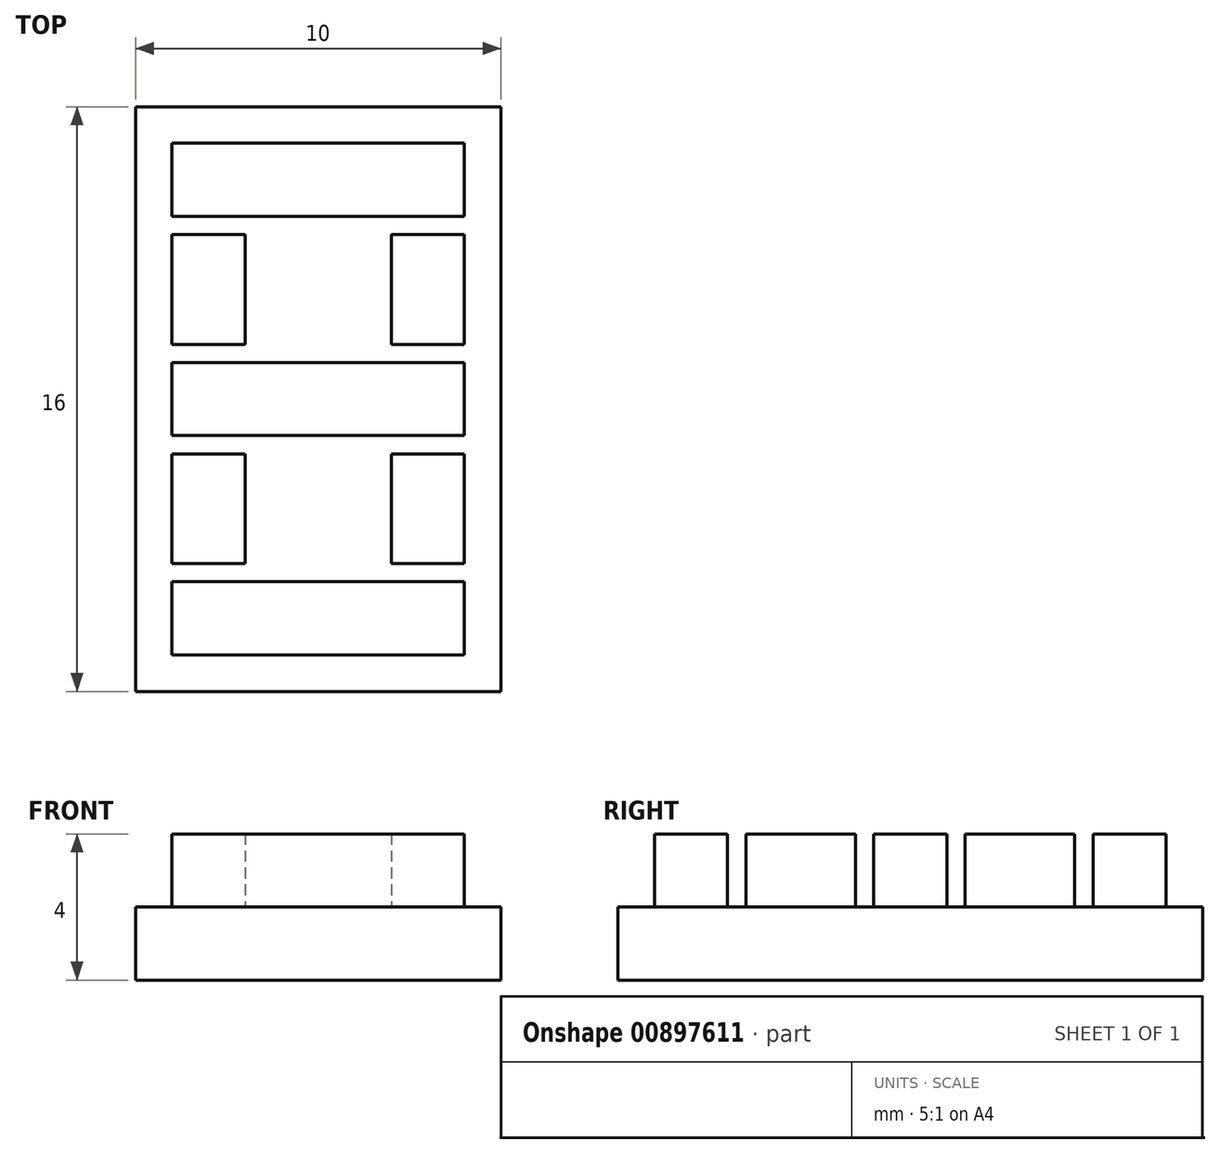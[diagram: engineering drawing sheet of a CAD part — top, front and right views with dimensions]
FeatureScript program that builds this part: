
annotation { "Feature Type Name" : "Feature", "Feature Type Description" : "" }
export const myFeature = defineFeature(function(context is Context, id is Id, definition is map)
    precondition{}
    {
        {
            var Q0;
            Q0=qCreatedBy(makeId("Top.planeOp"),FACE);
            var sketch = newSketch(context, id + "F0", { "sketchPlane" : qUnion([Q0])});
            skLineSegment(sketch, "E0.bottom", {"start": v(5, -8) * mm, "end": v(-5, -8) * mm});
            skLineSegment(sketch, "E0.top", {"start": v(5, 8) * mm, "end": v(-5, 8) * mm});
            skLineSegment(sketch, "E0.left", {"start": v(5, -8) * mm, "end": v(5, 8) * mm});
            skLineSegment(sketch, "E0.right", {"start": v(-5, -8) * mm, "end": v(-5, 8) * mm});
            skPoint(sketch, "E0.middle", {"position": v(0, 0) * mm});
            skSolve(sketch);
        }
        {
            var Q0;
            Q0=makeQuery(id+"F0.imprint","IMPRINT",FACE,{"disambiguationData":[TD([[makeQuery(id+"F0.imprint","IMPRINT",EDGE,{"derivedFrom":sQuery(id+"F0.wireOp",EDGE,"E0.bottom")}),-1.0]])]});
            extrude(context, id + "F1", {"entities" : qUnion([Q0]), "depth" : 2 * mm, "offsetDistance" : 25 * mm});
        }
        {
            var Q0;
            Q0=makeQuery(id+"F1.opExtrude","CAP_FACE",FACE,{"disambiguationData":[OSD([sQuery(id+"F0.wireOp",EDGE,"E0.bottom"),sQuery(id+"F0.wireOp",EDGE,"E0.top"),sQuery(id+"F0.wireOp",EDGE,"E0.left"),sQuery(id+"F0.wireOp",EDGE,"E0.right")])],"isStart":false});
            var sketch = newSketch(context, id + "F2", { "sketchPlane" : qUnion([Q0])});
            skLineSegment(sketch, "E1.top", {"start": v(4, 1) * mm, "end": v(-4, 1) * mm});
            skLineSegment(sketch, "E1.left", {"start": v(4, -1) * mm, "end": v(4, 1) * mm});
            skLineSegment(sketch, "E1.right", {"start": v(-4, -1) * mm, "end": v(-4, 1) * mm});
            skPoint(sketch, "E1.middle", {"position": v(0, 0) * mm});
            skPoint(sketch, "E2.middle", {"position": v(0, 6) * mm});
            skLineSegment(sketch, "E3", {"start": v(0, 8) * mm, "end": v(0, -8) * mm, "construction": true});
            skLineSegment(sketch, "E4.bottom", {"start": v(4, -7) * mm, "end": v(-4, -7) * mm});
            skLineSegment(sketch, "E4.top", {"start": v(4, -5) * mm, "end": v(-4, -5) * mm});
            skLineSegment(sketch, "E4.left", {"start": v(4, -7) * mm, "end": v(4, -5) * mm});
            skLineSegment(sketch, "E4.right", {"start": v(-4, -7) * mm, "end": v(-4, -5) * mm});
            skPoint(sketch, "E4.middle", {"position": v(0, -6) * mm});
            skLineSegment(sketch, "E5.bottom", {"start": v(-4, 4.5) * mm, "end": v(-2, 4.5) * mm});
            skLineSegment(sketch, "E5.top", {"start": v(-4, 1.5) * mm, "end": v(-2, 1.5) * mm});
            skLineSegment(sketch, "E5.left", {"start": v(-4, 4.5) * mm, "end": v(-4, 1.5) * mm});
            skLineSegment(sketch, "E5.right", {"start": v(-2, 4.5) * mm, "end": v(-2, 1.5) * mm});
            skLineSegment(sketch, "E6.MirrorCS", {"start": v(4, 1.5) * mm, "end": v(2, 1.5) * mm});
            skLineSegment(sketch, "E7.MirrorCS", {"start": v(2, 4.5) * mm, "end": v(2, 1.5) * mm});
            skLineSegment(sketch, "E8.MirrorCS", {"start": v(4, 4.5) * mm, "end": v(2, 4.5) * mm});
            skLineSegment(sketch, "E9.MirrorCS", {"start": v(4, 4.5) * mm, "end": v(4, 1.5) * mm});
            skLineSegment(sketch, "E10.MirrorCS", {"start": v(-4, -4.5) * mm, "end": v(-2, -4.5) * mm});
            skLineSegment(sketch, "E11.MirrorCS", {"start": v(-2, -4.5) * mm, "end": v(-2, -1.5) * mm});
            skLineSegment(sketch, "E12.MirrorCS", {"start": v(-4, -4.5) * mm, "end": v(-4, -1.5) * mm});
            skLineSegment(sketch, "E13.MirrorCS", {"start": v(-4, -1.5) * mm, "end": v(-2, -1.5) * mm});
            skLineSegment(sketch, "E14.MirrorCS", {"start": v(4, -4.5) * mm, "end": v(2, -4.5) * mm});
            skLineSegment(sketch, "E15.MirrorCS", {"start": v(2, -4.5) * mm, "end": v(2, -1.5) * mm});
            skLineSegment(sketch, "E16.MirrorCS", {"start": v(4, -1.5) * mm, "end": v(2, -1.5) * mm});
            skLineSegment(sketch, "E17.MirrorCS", {"start": v(4, -4.5) * mm, "end": v(4, -1.5) * mm});
            skLineSegment(sketch, "E18", {"start": v(-4, -1) * mm, "end": v(4, -1) * mm});
            skLineSegment(sketch, "E19.MirrorCS", {"start": v(4, 5) * mm, "end": v(-4, 5) * mm});
            skLineSegment(sketch, "E20.MirrorCS", {"start": v(-4, 7) * mm, "end": v(-4, 5) * mm});
            skLineSegment(sketch, "E21.MirrorCS", {"start": v(4, 7) * mm, "end": v(-4, 7) * mm});
            skLineSegment(sketch, "E22.MirrorCS", {"start": v(4, 7) * mm, "end": v(4, 5) * mm});
            skSolve(sketch);
        }
        {
            var Q0;
            Q0 = qSketchRegion(id + "F2", true);
            extrude(context, id + "F3", {"entities" : qUnion([Q0]), "operationType" : NewBodyOperationType.ADD, "depth" : 2 * mm, "offsetDistance" : 25 * mm});
        }
    });
